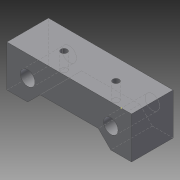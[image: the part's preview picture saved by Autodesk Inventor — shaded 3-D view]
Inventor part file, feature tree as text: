
AUTODESK INVENTOR PART (.ipt)
format: ipt  version: 2015 (Build 190159000, 159)  size: 118,784 bytes
history: native  units: mm
features: sketch x5, extrude x3, hole x1, chamfer x1
ambient origin geometry x8: Origin, YZ Plane, XZ Plane, XY Plane, X Axis, Y Axis, Z Axis, Center Point
bodies: Solid1 (feature_tree)
feature tree (10):
  extrude  "Extrusion1"  Depth=20.0mm
  extrude  "Extrusion2"  Depth=20.0mm
  hole  "Hole1"  [1 undecoded]
  extrude  "Extrusion3"  Depth=10.0mm
  chamfer  "Chamfer1"  Distance=20.0mm
  sketch  "Sketch5"  dims[d9=7.0mm d10=20.0mm d11=0.0mm d12=10.0mm d13=10.0mm d14=25.0mm d15=17.5mm d16=17.5mm d17=3.0mm d18=6.0mm d19=4.0mm d20=2.0mm d21=90.0deg d22=8.0mm d23=20.594885mm d24=16.0mm d25=16.0mm d26=6.0mm d27=20.0mm d28=0.0mm d29=6.0mm d30=2.0mm d31=45.0deg]
  sketch  "Sketch1"  dims[d0=60.0mm d1=20.0mm]
  sketch  "Sketch2"  dims[d2=20.0mm d3=0.0mm d4=40.0mm]
  sketch  "Sketch3"  dims[d5=10.0mm d6=10.0mm]
  sketch  "Sketch4"  dims[d7=10.0mm d8=7.0mm]
note: 1 required parameter value undecoded (feature->parameter linkage not recoverable at this tier; creation-order binding heuristic only, values carry confidence <= 0.55)
